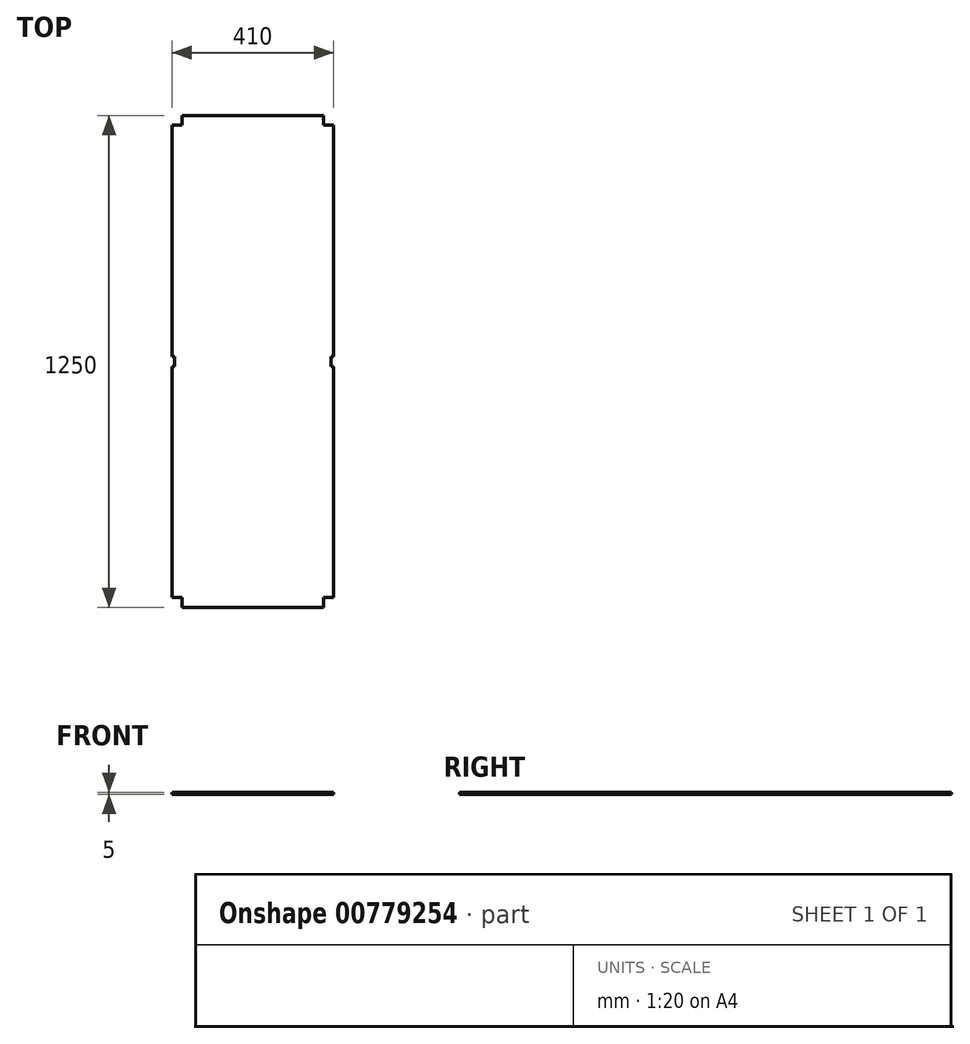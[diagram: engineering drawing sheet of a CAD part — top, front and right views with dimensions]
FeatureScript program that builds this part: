
annotation { "Feature Type Name" : "Feature", "Feature Type Description" : "" }
export const myFeature = defineFeature(function(context is Context, id is Id, definition is map)
    precondition{}
    {
        {
            var Q0;
            Q0=qCreatedBy(makeId("Top.planeOp"),FACE);
            var sketch = newSketch(context, id + "F0", { "sketchPlane" : qUnion([Q0])});
            skLineSegment(sketch, "E0.bottom", {"start": v(0, 0) * mm, "end": v(410, 0) * mm});
            skLineSegment(sketch, "E0.top", {"start": v(0, 1250) * mm, "end": v(410, 1250) * mm});
            skLineSegment(sketch, "E0.left", {"start": v(0, 0) * mm, "end": v(0, 1250) * mm});
            skLineSegment(sketch, "E0.right", {"start": v(410, 0) * mm, "end": v(410, 1250) * mm});
            skSolve(sketch);
        }
        {
            var Q0;
            Q0=qSketchRegion(id+"F0",true);
            extrude(context, id + "F1", {"entities" : qUnion([Q0]), "depth" : 5 * mm});
        }
        {
            var Q0;
            Q0=makeQuery(id+"F1.opExtrude","CAP_FACE",FACE,{"disambiguationData":[OSD([sQuery(id+"F0.wireOp",EDGE,"E0.bottom"),sQuery(id+"F0.wireOp",EDGE,"E0.top"),sQuery(id+"F0.wireOp",EDGE,"E0.left"),sQuery(id+"F0.wireOp",EDGE,"E0.right")])],"isStart":false});
            var sketch = newSketch(context, id + "F2", { "sketchPlane" : qUnion([Q0])});
            skLineSegment(sketch, "E1.bottom", {"start": v(0, 0) * mm, "end": v(25, 0) * mm});
            skLineSegment(sketch, "E1.top", {"start": v(0, 25) * mm, "end": v(25, 25) * mm});
            skLineSegment(sketch, "E1.left", {"start": v(0, 0) * mm, "end": v(0, 25) * mm});
            skLineSegment(sketch, "E1.right", {"start": v(25, 0) * mm, "end": v(25, 25) * mm});
            skSolve(sketch);
        }
        {
            var Q0;
            Q0=qSketchRegion(id+"F2",true);
            extrude(context, id + "F3", {"entities" : qUnion([Q0]), "operationType" : NewBodyOperationType.REMOVE, "oppositeDirection" : true, "depth" : 25 * mm});
        }
        {
            var Q0;
            Q0=makeQuery(id+"F1.opExtrude","CAP_FACE",FACE,{"disambiguationData":[OSD([sQuery(id+"F0.wireOp",EDGE,"E0.bottom"),sQuery(id+"F0.wireOp",EDGE,"E0.top"),sQuery(id+"F0.wireOp",EDGE,"E0.left"),sQuery(id+"F0.wireOp",EDGE,"E0.right")])],"isStart":false});
            var sketch = newSketch(context, id + "F4", { "sketchPlane" : qUnion([Q0])});
            skLineSegment(sketch, "E2.bottom", {"start": v(410, 0) * mm, "end": v(385, 0) * mm});
            skLineSegment(sketch, "E2.top", {"start": v(410, 25) * mm, "end": v(385, 25) * mm});
            skLineSegment(sketch, "E2.left", {"start": v(410, 0) * mm, "end": v(410, 25) * mm});
            skLineSegment(sketch, "E2.right", {"start": v(385, 0) * mm, "end": v(385, 25) * mm});
            skSolve(sketch);
        }
        {
            var Q0;
            Q0=qSketchRegion(id+"F4",true);
            extrude(context, id + "F5", {"entities" : qUnion([Q0]), "operationType" : NewBodyOperationType.REMOVE, "oppositeDirection" : true, "depth" : 25 * mm});
        }
        {
            var Q0;
            Q0=makeQuery(id+"F1.opExtrude","CAP_FACE",FACE,{"disambiguationData":[OSD([sQuery(id+"F0.wireOp",EDGE,"E0.bottom"),sQuery(id+"F0.wireOp",EDGE,"E0.top"),sQuery(id+"F0.wireOp",EDGE,"E0.left"),sQuery(id+"F0.wireOp",EDGE,"E0.right")])],"isStart":false});
            var sketch = newSketch(context, id + "F6", { "sketchPlane" : qUnion([Q0])});
            skLineSegment(sketch, "E3.bottom", {"start": v(410, 1250) * mm, "end": v(385, 1250) * mm});
            skLineSegment(sketch, "E3.top", {"start": v(410, 1225) * mm, "end": v(385, 1225) * mm});
            skLineSegment(sketch, "E3.left", {"start": v(410, 1250) * mm, "end": v(410, 1225) * mm});
            skLineSegment(sketch, "E3.right", {"start": v(385, 1250) * mm, "end": v(385, 1225) * mm});
            skSolve(sketch);
        }
        {
            var Q0;
            Q0=qSketchRegion(id+"F6",true);
            extrude(context, id + "F7", {"entities" : qUnion([Q0]), "operationType" : NewBodyOperationType.REMOVE, "oppositeDirection" : true, "depth" : 25 * mm});
        }
        {
            var Q0;
            Q0=makeQuery(id+"F1.opExtrude","CAP_FACE",FACE,{"disambiguationData":[OSD([sQuery(id+"F0.wireOp",EDGE,"E0.bottom"),sQuery(id+"F0.wireOp",EDGE,"E0.top"),sQuery(id+"F0.wireOp",EDGE,"E0.left"),sQuery(id+"F0.wireOp",EDGE,"E0.right")])],"isStart":false});
            var sketch = newSketch(context, id + "F8", { "sketchPlane" : qUnion([Q0])});
            skLineSegment(sketch, "E4.bottom", {"start": v(0, 1250) * mm, "end": v(25, 1250) * mm});
            skLineSegment(sketch, "E4.top", {"start": v(0, 1225) * mm, "end": v(25, 1225) * mm});
            skLineSegment(sketch, "E4.left", {"start": v(0, 1250) * mm, "end": v(0, 1225) * mm});
            skLineSegment(sketch, "E4.right", {"start": v(25, 1250) * mm, "end": v(25, 1225) * mm});
            skSolve(sketch);
        }
        {
            var Q0;
            Q0=makeQuery(id+"F8.imprint","IMPRINT",FACE,{"disambiguationData":[TD([[makeQuery(id+"F8.imprint","IMPRINT",EDGE,{"derivedFrom":sQuery(id+"F8.wireOp",EDGE,"E4.bottom")}),-1.0]])]});
            extrude(context, id + "F9", {"entities" : qUnion([Q0]), "operationType" : NewBodyOperationType.REMOVE, "oppositeDirection" : true, "depth" : 25 * mm});
        }
        {
            var Q0;
            Q0=makeQuery(id+"F1.opExtrude","CAP_FACE",FACE,{"disambiguationData":[OSD([sQuery(id+"F0.wireOp",EDGE,"E0.bottom"),sQuery(id+"F0.wireOp",EDGE,"E0.top"),sQuery(id+"F0.wireOp",EDGE,"E0.left"),sQuery(id+"F0.wireOp",EDGE,"E0.right")])],"isStart":false});
            var sketch = newSketch(context, id + "F10", { "sketchPlane" : qUnion([Q0])});
            skLineSegment(sketch, "E5.bottom", {"start": v(6, 638) * mm, "end": v(-6, 638) * mm});
            skLineSegment(sketch, "E5.top", {"start": v(6, 612) * mm, "end": v(-6, 612) * mm});
            skLineSegment(sketch, "E5.left", {"start": v(-6, 638) * mm, "end": v(-6, 612) * mm});
            skLineSegment(sketch, "E5.right", {"start": v(6, 638) * mm, "end": v(6, 612) * mm});
            skPoint(sketch, "E5.middle", {"position": v(0, 625) * mm});
            skSolve(sketch);
        }
        {
            var Q0;
            Q0=qSketchRegion(id+"F10",true);
            extrude(context, id + "F11", {"entities" : qUnion([Q0]), "operationType" : NewBodyOperationType.REMOVE, "oppositeDirection" : true, "depth" : 25 * mm});
        }
        {
            var Q0;
            Q0=makeQuery(id+"F1.opExtrude","CAP_FACE",FACE,{"disambiguationData":[OSD([sQuery(id+"F0.wireOp",EDGE,"E0.bottom"),sQuery(id+"F0.wireOp",EDGE,"E0.top"),sQuery(id+"F0.wireOp",EDGE,"E0.left"),sQuery(id+"F0.wireOp",EDGE,"E0.right")])],"isStart":false});
            var sketch = newSketch(context, id + "F12", { "sketchPlane" : qUnion([Q0])});
            skLineSegment(sketch, "E6.bottom", {"start": v(404, 638) * mm, "end": v(416, 638) * mm});
            skLineSegment(sketch, "E6.top", {"start": v(404, 612) * mm, "end": v(416, 612) * mm});
            skLineSegment(sketch, "E6.left", {"start": v(404, 638) * mm, "end": v(404, 612) * mm});
            skLineSegment(sketch, "E6.right", {"start": v(416, 638) * mm, "end": v(416, 612) * mm});
            skPoint(sketch, "E6.middle", {"position": v(410, 625) * mm});
            skSolve(sketch);
        }
        {
            var Q0;
            Q0=qSketchRegion(id+"F12",true);
            extrude(context, id + "F13", {"entities" : qUnion([Q0]), "operationType" : NewBodyOperationType.REMOVE, "oppositeDirection" : true, "depth" : 25 * mm});
        }
    });
